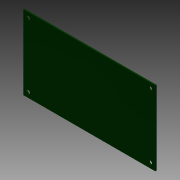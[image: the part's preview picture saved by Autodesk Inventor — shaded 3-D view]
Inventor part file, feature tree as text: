
AUTODESK INVENTOR PART (.ipt)
format: ipt  version: 2013 (Build 170138000, 138)  size: 123,904 bytes
history: native  units: in
note: dims shown in document units (in); Inventor stores cm internally (conversion verified against a paired STEP export)
features: extrude x2, sketch x2
ambient origin geometry x8: Origin, YZ Plane, XZ Plane, XY Plane, X Axis, Y Axis, Z Axis, Center Point
bodies: Solid1 (feature_tree)
feature tree (4):
  extrude  "Extrusion1"  Depth=4.0in
  extrude  "Extrusion3"  Depth=1.95in
  sketch  "Sketch1"  dims[d0=0.0394in d1=0.0in d2=4.0in]
  sketch  "Sketch3"  dims[d4=2.25in d5=1.95in d6=0.1102in d8=0.1102in d10=1.95in d15=0.0787in d16=0.1969in d17=0.1969in d18=0.0394in d19=0.1181in d20=0.0in d21=0.15in d22=0.15in d23=0.15in d24=0.15in d25=0.15in d26=0.15in d27=0.15in d28=0.15in d29=0.8in d30=2.1in d31=1.95in d32=3.7in d33=1.1469in d34=1.1469in]
